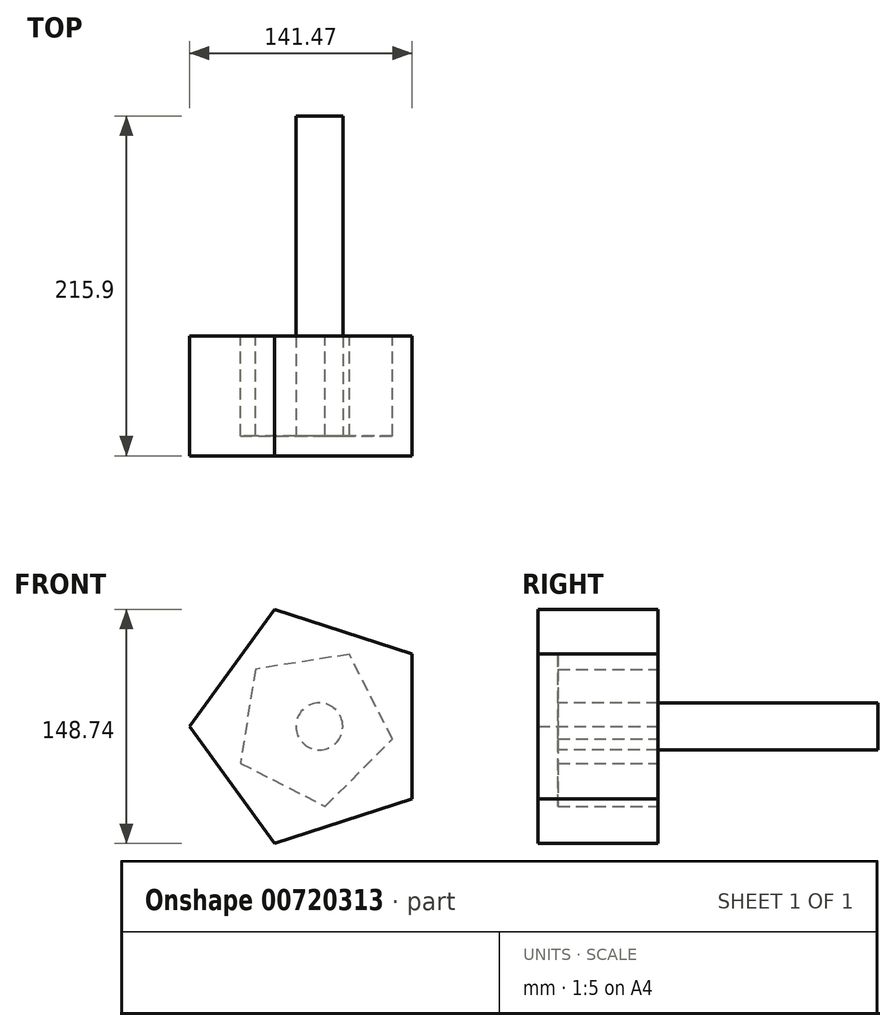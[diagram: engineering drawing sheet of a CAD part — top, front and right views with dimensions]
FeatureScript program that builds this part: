
annotation { "Feature Type Name" : "Feature", "Feature Type Description" : "" }
export const myFeature = defineFeature(function(context is Context, id is Id, definition is map)
    precondition{}
    {
        {
            var Q0;
            Q0=qCreatedBy(makeId("Front.planeOp"),FACE);
            var sketch = newSketch(context, id + "F0", { "sketchPlane" : qUnion([Q0])});
            skCircle(sketch, "E0.cCircle", {"center": v(0, 0) * mm, "radius": 78.2 * mm, "construction": true});
            skLineSegment(sketch, "E0.0", {"start": v(-78.2, 0) * mm, "end": v(-24.17, 74.37) * mm});
            skLineSegment(sketch, "E0.1", {"start": v(-24.17, 74.37) * mm, "end": v(63.27, 45.97) * mm});
            skLineSegment(sketch, "E0.2", {"start": v(63.27, 45.97) * mm, "end": v(63.27, -45.97) * mm});
            skLineSegment(sketch, "E0.3", {"start": v(63.27, -45.97) * mm, "end": v(-24.17, -74.37) * mm});
            skLineSegment(sketch, "E0.4", {"start": v(-24.17, -74.37) * mm, "end": v(-78.2, 0) * mm});
            skSolve(sketch);
        }
        {
            var Q0;
            Q0 = qSketchRegion(id + "F0", true);
            extrude(context, id + "F1", {"entities" : qUnion([Q0]), "depth" : 76.2 * mm, "offsetDistance" : 25.4 * mm});
        }
        {
            var Q0;
            Q0=makeQuery(id+"F1.opExtrude","CAP_FACE",FACE,{"disambiguationData":[OSD([sQuery(id+"F0.wireOp",EDGE,"E0.0"),sQuery(id+"F0.wireOp",EDGE,"E0.1"),sQuery(id+"F0.wireOp",EDGE,"E0.2"),sQuery(id+"F0.wireOp",EDGE,"E0.3"),sQuery(id+"F0.wireOp",EDGE,"E0.4")])],"isStart":true});
            var sketch = newSketch(context, id + "F2", { "sketchPlane" : qUnion([Q0])});
            skCircle(sketch, "E1.cCircle", {"center": v(0, 0) * mm, "radius": 51.4 * mm, "construction": true});
            skLineSegment(sketch, "E1.0", {"start": v(-50.76, -8.05) * mm, "end": v(-23.34, 45.8) * mm});
            skLineSegment(sketch, "E1.1", {"start": v(-23.34, 45.8) * mm, "end": v(36.34, 36.35) * mm});
            skLineSegment(sketch, "E1.2", {"start": v(36.34, 36.35) * mm, "end": v(45.8, -23.33) * mm});
            skLineSegment(sketch, "E1.3", {"start": v(45.8, -23.33) * mm, "end": v(-8.03, -50.76) * mm});
            skLineSegment(sketch, "E1.4", {"start": v(-8.03, -50.76) * mm, "end": v(-50.76, -8.05) * mm});
            skSolve(sketch);
        }
        {
            var Q0;
            Q0=makeQuery(id+"F2.imprint","IMPRINT",FACE,{"disambiguationData":[TD([[makeQuery(id+"F2.imprint","IMPRINT",EDGE,{"derivedFrom":sQuery(id+"F2.wireOp",EDGE,"E1.0")}),-1.0]])]});
            extrude(context, id + "F3", {"entities" : qUnion([Q0]), "operationType" : NewBodyOperationType.REMOVE, "oppositeDirection" : true, "depth" : 63.5 * mm, "offsetDistance" : 25.4 * mm});
        }
        {
            var Q0;
            Q0=makeQuery(id+"F3.boolean.opBoolean","COPY",FACE,{"derivedFrom":makeQuery(id+"F3.opExtrude","CAP_FACE",FACE,{"disambiguationData":[OSD([sQuery(id+"F2.wireOp",EDGE,"E1.0"),sQuery(id+"F2.wireOp",EDGE,"E1.1"),sQuery(id+"F2.wireOp",EDGE,"E1.2"),sQuery(id+"F2.wireOp",EDGE,"E1.3"),sQuery(id+"F2.wireOp",EDGE,"E1.4")])],"isStart":false})});
            var sketch = newSketch(context, id + "F4", { "sketchPlane" : qUnion([Q0])});
            skCircle(sketch, "E2", {"center": v(-4.35, 0) * mm, "radius": 14.89 * mm});
            skSolve(sketch);
        }
        {
            var Q0;
            Q0 = qSketchRegion(id + "F4", true);
            extrude(context, id + "F5", {"entities" : qUnion([Q0]), "operationType" : NewBodyOperationType.ADD, "depth" : 203.2 * mm, "offsetDistance" : 25.4 * mm});
        }
    });
